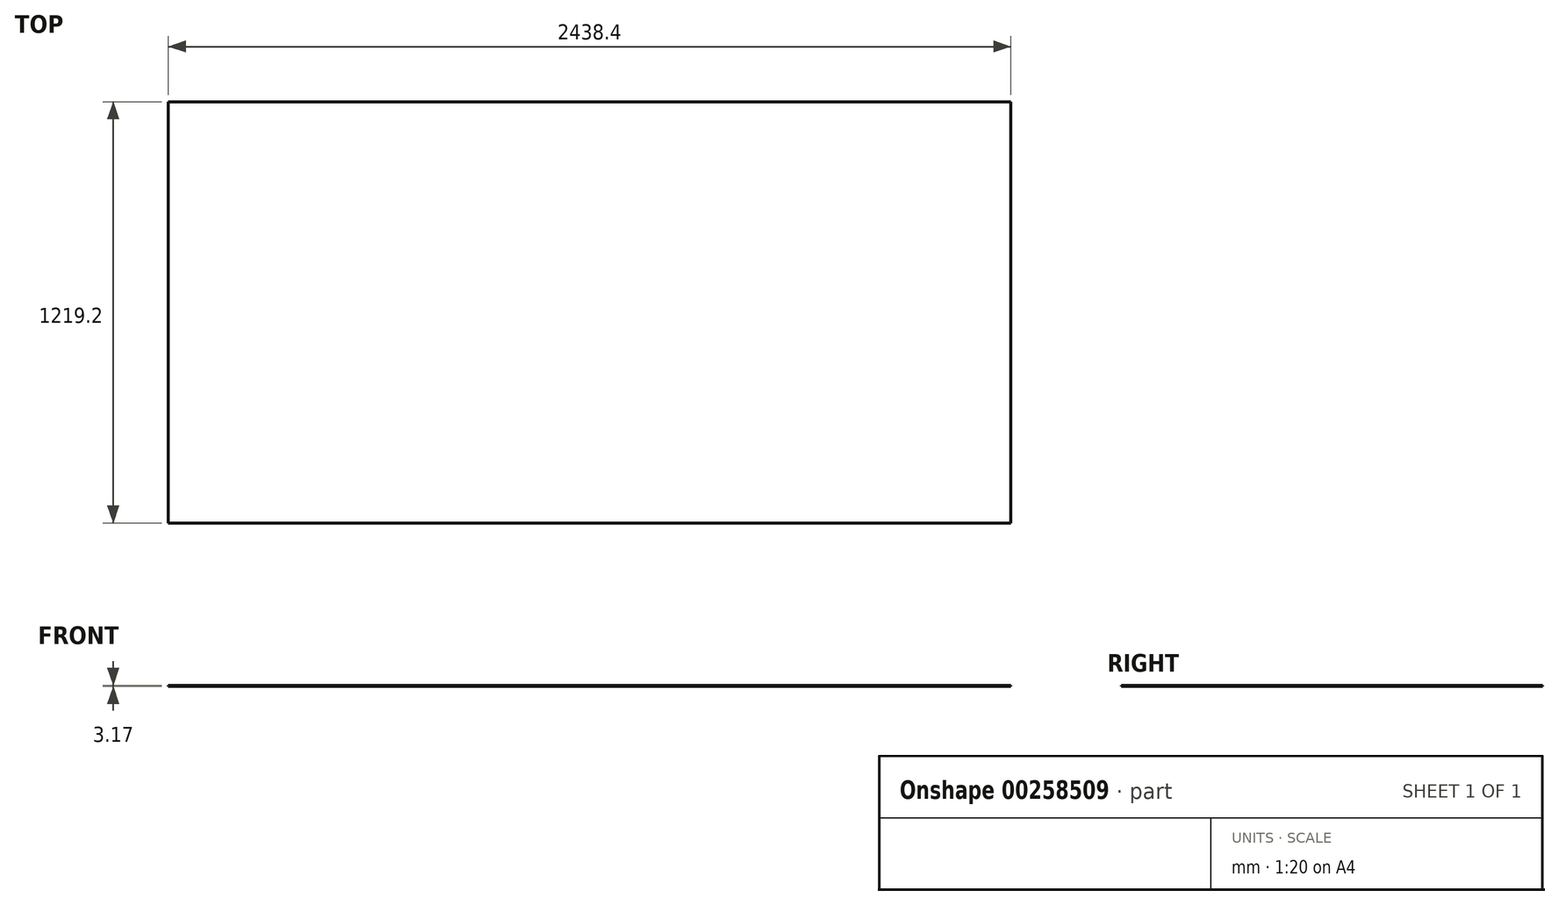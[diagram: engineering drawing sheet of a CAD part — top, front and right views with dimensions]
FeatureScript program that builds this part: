
annotation { "Feature Type Name" : "Feature", "Feature Type Description" : "" }
export const myFeature = defineFeature(function(context is Context, id is Id, definition is map)
    precondition{}
    {
        {
            var Q0;
            Q0=qCreatedBy(makeId("Top.planeOp"),FACE);
            var sketch = newSketch(context, id + "F0", { "sketchPlane" : qUnion([Q0])});
            skLineSegment(sketch, "E0.bottom", {"start": v(1219.2, -609.6) * mm, "end": v(-1219.2, -609.6) * mm});
            skLineSegment(sketch, "E0.top", {"start": v(1219.2, 609.6) * mm, "end": v(-1219.2, 609.6) * mm});
            skLineSegment(sketch, "E0.left", {"start": v(1219.2, -609.6) * mm, "end": v(1219.2, 609.6) * mm});
            skLineSegment(sketch, "E0.right", {"start": v(-1219.2, -609.6) * mm, "end": v(-1219.2, 609.6) * mm});
            skPoint(sketch, "E0.middle", {"position": v(0, 0) * mm});
            skSolve(sketch);
        }
        {
            var Q0;
            Q0 = qSketchRegion(id + "F0", true);
            extrude(context, id + "F1", {"entities" : qUnion([Q0]), "depth" : 3.17 * mm});
        }
    });
